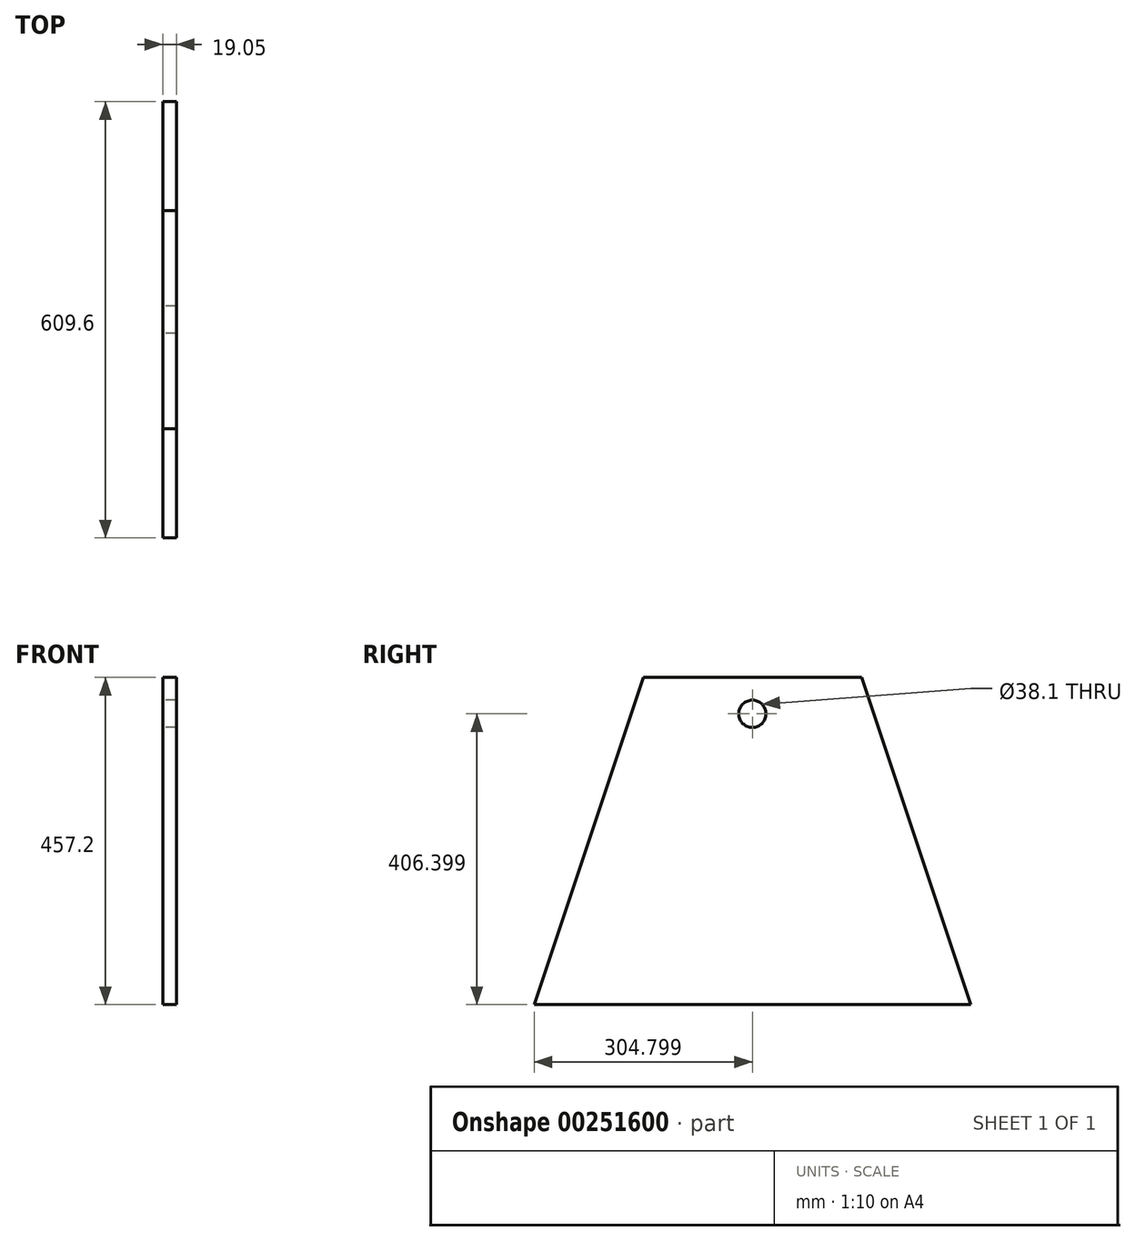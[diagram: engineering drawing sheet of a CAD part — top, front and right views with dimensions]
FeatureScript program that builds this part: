
annotation { "Feature Type Name" : "Feature", "Feature Type Description" : "" }
export const myFeature = defineFeature(function(context is Context, id is Id, definition is map)
    precondition{}
    {
        {
            var Q0;
            Q0=qCreatedBy(makeId("Right.planeOp"),FACE);
            var sketch = newSketch(context, id + "F0", { "sketchPlane" : qUnion([Q0])});
            skLineSegment(sketch, "E0", {"start": v(-272.91, -33.63) * mm, "end": v(31.89, -33.63) * mm});
            skLineSegment(sketch, "E1", {"start": v(-272.91, -33.63) * mm, "end": v(-425.31, -33.63) * mm});
            skLineSegment(sketch, "E2", {"start": v(31.89, -33.63) * mm, "end": v(184.29, -33.63) * mm});
            skLineSegment(sketch, "E3", {"start": v(-272.91, -33.63) * mm, "end": v(-272.91, 423.57) * mm, "construction": true});
            skLineSegment(sketch, "E4", {"start": v(-272.91, 423.57) * mm, "end": v(-425.31, -33.63) * mm});
            skLineSegment(sketch, "E5", {"start": v(-272.91, 423.57) * mm, "end": v(31.89, 423.57) * mm});
            skLineSegment(sketch, "E6", {"start": v(31.89, 423.57) * mm, "end": v(184.29, -33.63) * mm});
            skLineSegment(sketch, "E7", {"start": v(31.89, 423.57) * mm, "end": v(31.89, -33.63) * mm, "construction": true});
            skSolve(sketch);
        }
        {
            var Q0;
            Q0 = qSketchRegion(id + "F0", true);
            extrude(context, id + "F1", {"entities" : qUnion([Q0]), "depth" : 19.05 * mm});
        }
        {
            var Q0;
            Q0=makeQuery(id+"F0.imprint","IMPRINT",FACE,{"disambiguationData":[TD([[makeQuery(id+"F0.imprint","IMPRINT",EDGE,{"derivedFrom":sQuery(id+"F0.wireOp",EDGE,"E0")}),1.0]])]});
            var sketch = newSketch(context, id + "F2", { "sketchPlane" : qUnion([Q0])});
            skPoint(sketch, "E8", {"position": v(-120.51, 423.57) * mm});
            skCircle(sketch, "E9", {"center": v(-120.51, 372.77) * mm, "radius": 19.05 * mm});
            skSolve(sketch);
        }
        {
            var Q0;
            Q0=sQuery(id+"F2.wireOp",EDGE,"E9");
            extrude(context, id + "F3", {"bodyType" : ToolBodyType.SURFACE, "surfaceEntities" : qUnion([Q0]), "depth" : 19.05 * mm});
        }
        {
            var Q0;
            Q0=sQuery(id+"F2.wireOp",VERTEX,"E9.center");
            var Q1;
            Q1=makeQuery(id+"F1.opExtrude","SWEPT_BODY",BODY,{"disambiguationData":[OSD([sQuery(id+"F0.wireOp",EDGE,"E0"),sQuery(id+"F0.wireOp",EDGE,"E1"),sQuery(id+"F0.wireOp",EDGE,"E2"),sQuery(id+"F0.wireOp",EDGE,"E4"),sQuery(id+"F0.wireOp",EDGE,"E5"),sQuery(id+"F0.wireOp",EDGE,"E6")])]});
            hole(context, id + "F4", {"style" : HoleStyle.SIMPLE, "endStyle" : HoleEndStyle.THROUGH, "oppositeDirection" : true, "holeDiameter" : 38.1 * mm, "tappedDepth" : 12.7 * mm, "tapClearance" : 3, "locations" : qUnion([Q0]), "scope" : qUnion([Q1])});
        }
    });
